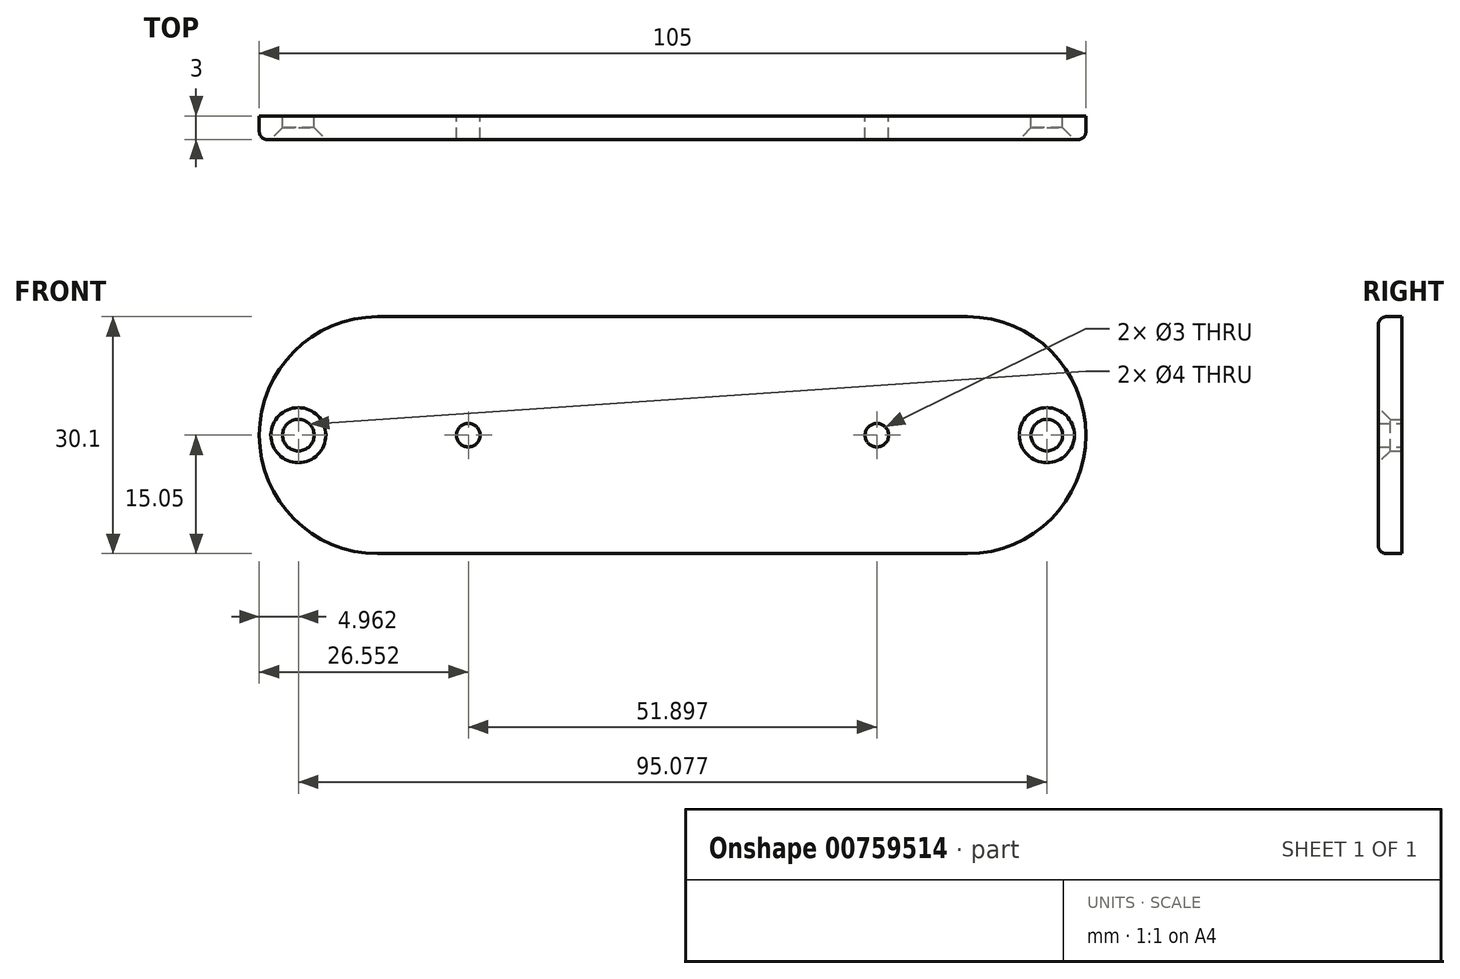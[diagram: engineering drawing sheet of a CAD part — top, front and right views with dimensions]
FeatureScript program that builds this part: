
annotation { "Feature Type Name" : "Feature", "Feature Type Description" : "" }
export const myFeature = defineFeature(function(context is Context, id is Id, definition is map)
    precondition{}
    {
        {
            var Q0;
            Q0=qCreatedBy(makeId("Front.planeOp"),FACE);
            var sketch = newSketch(context, id + "F0", { "sketchPlane" : qUnion([Q0])});
            skLineSegment(sketch, "E0.bottom", {"start": v(-37.45, 15.05) * mm, "end": v(37.45, 15.05) * mm});
            skLineSegment(sketch, "E0.top", {"start": v(-37.45, -15.05) * mm, "end": v(37.45, -15.05) * mm});
            skPoint(sketch, "E0.middle", {"position": v(0, 0) * mm});
            skArc(sketch, "E1", {"start": v(37.45, 15.05) * mm, "mid": v(52.5, 0) * mm, "end": v(37.45, -15.05) * mm});
            skPoint(sketch, "E2.center.orphan", {"position": v(-37.45, 0) * mm});
            skArc(sketch, "E3", {"start": v(-37.45, 15.05) * mm, "mid": v(-52.5, 0) * mm, "end": v(-37.45, -15.05) * mm});
            skCircle(sketch, "E4", {"center": v(-25.95, 0) * mm, "radius": 1.5 * mm});
            skCircle(sketch, "E5", {"center": v(-47.54, 0) * mm, "radius": 2 * mm});
            skCircle(sketch, "E6", {"center": v(25.95, 0) * mm, "radius": 1.5 * mm});
            skCircle(sketch, "E7", {"center": v(47.54, 0) * mm, "radius": 2 * mm});
            skSolve(sketch);
        }
        {
            var Q0;
            Q0=makeQuery(id+"F0.imprint","IMPRINT",FACE,{"disambiguationData":[TD([[makeQuery(id+"F0.imprint","IMPRINT",EDGE,{"derivedFrom":sQuery(id+"F0.wireOp",EDGE,"E0.bottom")}),-1.0]])]});
            extrude(context, id + "F1", {"entities" : qUnion([Q0]), "depth" : 3 * mm, "offsetDistance" : 25 * mm});
        }
        {
            var Q0;
            Q0=makeQuery(id+"F1.opExtrude","CAP_EDGE",EDGE,{"disambiguationData":[OSD([sQuery(id+"F0.wireOp",EDGE,"E0.bottom")])],"isStart":false});
            var Q1;
            Q1=makeQuery(id+"F1.opExtrude","CAP_EDGE",EDGE,{"disambiguationData":[OSD([sQuery(id+"F0.wireOp",EDGE,"E3")])],"isStart":false});
            var Q2;
            Q2=makeQuery(id+"F1.opExtrude","CAP_EDGE",EDGE,{"disambiguationData":[OSD([sQuery(id+"F0.wireOp",EDGE,"E0.top")])],"isStart":false});
            var Q3;
            Q3=makeQuery(id+"F1.opExtrude","CAP_EDGE",EDGE,{"disambiguationData":[OSD([sQuery(id+"F0.wireOp",EDGE,"E1")])],"isStart":false});
            fillet(context, id + "F2", {"entities" : qUnion([Q0, Q1, Q2, Q3]), "radius" : 1 * mm, "tangentPropagation" : true, "allowEdgeOverflow" : false});
        }
        {
            var Q0;
            Q0=makeQuery(id+"F1.opExtrude","CAP_EDGE",EDGE,{"disambiguationData":[OSD([sQuery(id+"F0.wireOp",EDGE,"E5")])],"isStart":false});
            chamfer(context, id + "F3", {"entities" : qUnion([Q0]), "width" : 1.5 * mm, "tangentPropagation" : true});
        }
        {
            var Q0;
            Q0=makeQuery(id+"F1.opExtrude","CAP_EDGE",EDGE,{"disambiguationData":[OSD([sQuery(id+"F0.wireOp",EDGE,"E7")])],"isStart":false});
            chamfer(context, id + "F4", {"entities" : qUnion([Q0]), "width" : 1.5 * mm, "tangentPropagation" : true});
        }
    });
